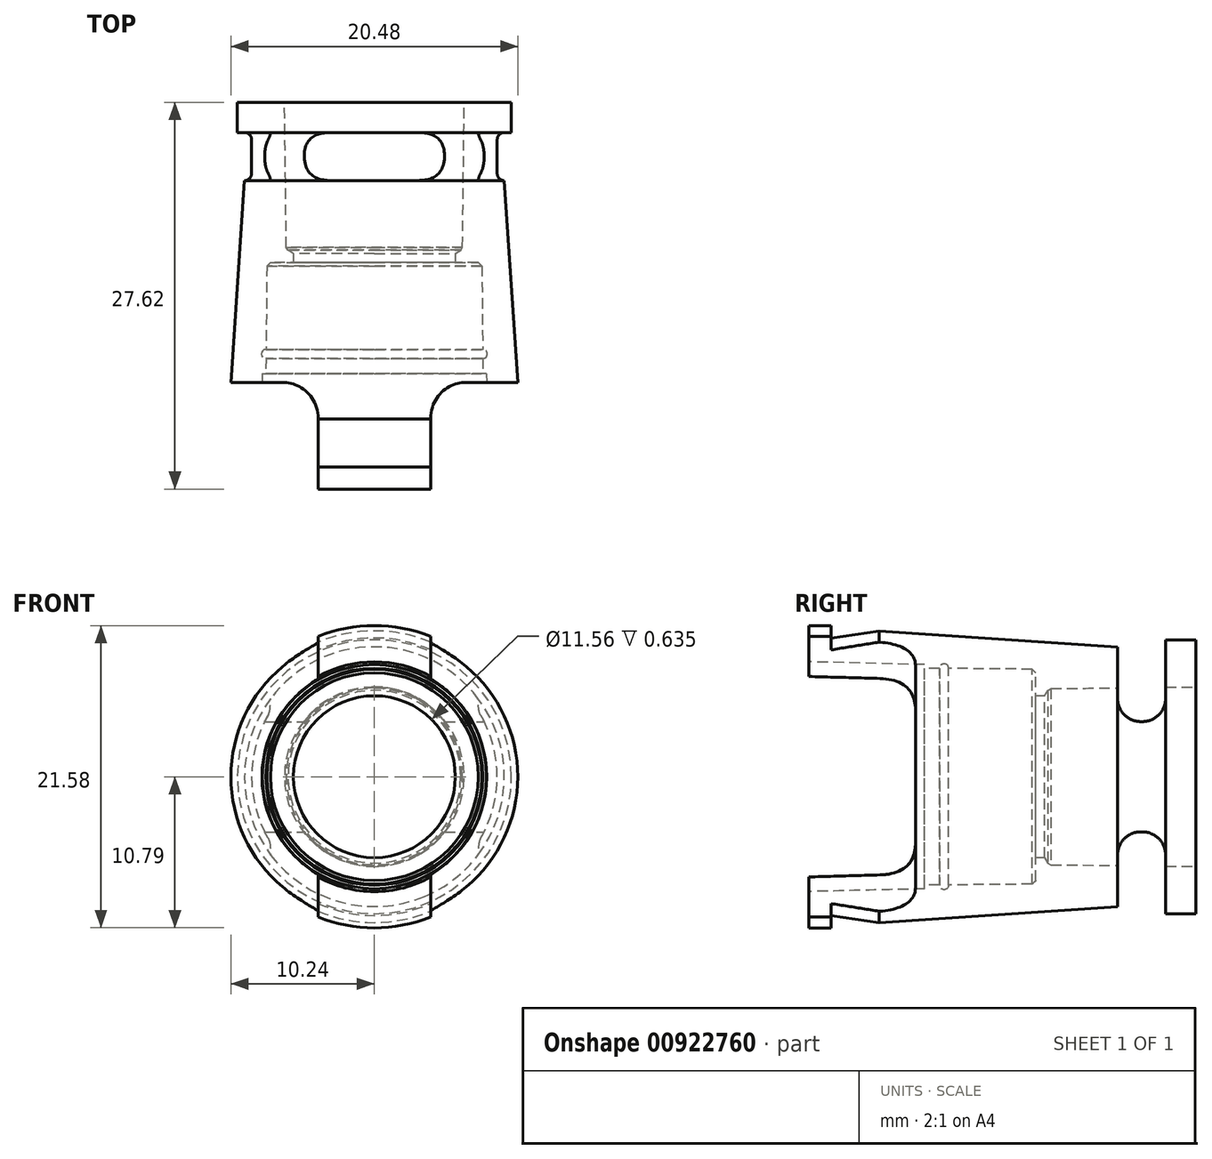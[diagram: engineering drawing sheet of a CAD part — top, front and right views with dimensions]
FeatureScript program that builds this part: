
annotation { "Feature Type Name" : "Feature", "Feature Type Description" : "" }
export const myFeature = defineFeature(function(context is Context, id is Id, definition is map)
    precondition{}
    {
        {
            var Q0;
            Q0=qCreatedBy(makeId("Right.planeOp"),FACE);
            var sketch = newSketch(context, id + "F0", { "sketchPlane" : qUnion([Q0])});
            skLineSegment(sketch, "E0.bottom", {"start": v(6.35, 6.41) * mm, "end": v(-6.35, 6.41) * mm, "construction": true});
            skLineSegment(sketch, "E0.top", {"start": v(6.35, -6.41) * mm, "end": v(-6.35, -6.41) * mm, "construction": true});
            skLineSegment(sketch, "E0.left", {"start": v(6.35, 6.41) * mm, "end": v(6.35, -6.41) * mm, "construction": true});
            skLineSegment(sketch, "E0.right", {"start": v(-6.35, 6.41) * mm, "end": v(-6.35, -6.41) * mm, "construction": true});
            skPoint(sketch, "E0.middle", {"position": v(0, 0) * mm});
            skLineSegment(sketch, "E1", {"start": v(-6.35, 6.41) * mm, "end": v(-6.35, 7.75) * mm});
            skLineSegment(sketch, "E2", {"start": v(-6.35, 6.41) * mm, "end": v(6.35, 6.41) * mm});
            skLineSegment(sketch, "E3", {"start": v(-6.35, 7.75) * mm, "end": v(-14.29, 7.75) * mm});
            skLineSegment(sketch, "E4", {"start": v(-14.29, 7.75) * mm, "end": v(-14.29, 8.2) * mm});
            skLineSegment(sketch, "E5", {"start": v(-14.29, 8.2) * mm, "end": v(-22.54, 8.2) * mm});
            skLineSegment(sketch, "E6", {"start": v(-6.35, 9.27) * mm, "end": v(-22.54, 9.27) * mm});
            skLineSegment(sketch, "E7", {"start": v(-22.54, 8.2) * mm, "end": v(-22.54, 9.27) * mm});
            skLineSegment(sketch, "E8", {"start": v(-6.35, 9.27) * mm, "end": v(6.35, 9.27) * mm});
            skLineSegment(sketch, "E9.bottom", {"start": v(-0.5, 8.76) * mm, "end": v(2.92, 8.76) * mm});
            skLineSegment(sketch, "E9.top", {"start": v(-0.5, 10.8) * mm, "end": v(2.92, 10.8) * mm});
            skLineSegment(sketch, "E9.left", {"start": v(-0.5, 8.76) * mm, "end": v(-0.5, 10.8) * mm});
            skLineSegment(sketch, "E9.right", {"start": v(2.92, 8.76) * mm, "end": v(2.92, 10.8) * mm});
            skLineSegment(sketch, "E10", {"start": v(0, 0) * mm, "end": v(6.35, 0) * mm});
            skLineSegment(sketch, "E11", {"start": v(-6.35, 6.41) * mm, "end": v(-6.35, 5.78) * mm});
            skLineSegment(sketch, "E12", {"start": v(-6.35, 5.78) * mm, "end": v(-5.72, 5.78) * mm});
            skLineSegment(sketch, "E13", {"start": v(-5.72, 5.78) * mm, "end": v(-5.33, 6.41) * mm});
            skLineSegment(sketch, "E14", {"start": v(5.08, 6.41) * mm, "end": v(5.08, 9.27) * mm});
            skLineSegment(sketch, "E15", {"start": v(-6.35, 7.67) * mm, "end": v(-14.29, 7.75) * mm});
            skLineSegment(sketch, "E16", {"start": v(-14.29, 8) * mm, "end": v(-22.54, 8.2) * mm});
            skLineSegment(sketch, "E17", {"start": v(-5.41, 6.29) * mm, "end": v(5.08, 6.41) * mm});
            skLineSegment(sketch, "E18", {"start": v(-22.54, 9.27) * mm, "end": v(-22.54, 10.8) * mm});
            skLineSegment(sketch, "E19", {"start": v(-22.54, 10.8) * mm, "end": v(-20.96, 10.8) * mm});
            skLineSegment(sketch, "E20", {"start": v(-20.96, 10.8) * mm, "end": v(-20.96, 9.27) * mm});
            skLineSegment(sketch, "E21", {"start": v(-17.53, 9.27) * mm, "end": v(-17.53, 10.41) * mm});
            skLineSegment(sketch, "E22", {"start": v(-17.53, 10.41) * mm, "end": v(-0.5, 9.27) * mm});
            skLineSegment(sketch, "E23", {"start": v(2.92, 9.78) * mm, "end": v(5.08, 9.78) * mm});
            skLineSegment(sketch, "E24", {"start": v(5.08, 9.78) * mm, "end": v(5.08, 9.27) * mm});
            skLineSegment(sketch, "E25", {"start": v(-17.53, 10.41) * mm, "end": v(-20.96, 9.9) * mm});
            skCircle(sketch, "E26", {"center": v(-12.9, 7.75) * mm, "radius": 0.32 * mm});
            skSolve(sketch);
        }
        {
            var Q0;
            Q0=makeQuery(id+"F0.imprint","IMPRINT",FACE,{"disambiguationData":[TD([[makeQuery(id+"F0.imprint","IMPRINT",EDGE,{"derivedFrom":sQuery(id+"F0.wireOp",EDGE,"E1")}),-1.0]])]});
            var Q1;
            {var subQ0=sQuery(id+"F0.wireOp",EDGE,"E11");Q1=makeQuery(id+"F0.imprint","IMPRINT",FACE,{"disambiguationData":[TD([[makeQuery(id+"F0.imprint","IMPRINT",EDGE,{"derivedFrom":subQ0}),1.0]])]});}
            var Q2;
            {var subQ3=sQuery(id+"F0.wireOp",EDGE,"E17");Q2=makeQuery(id+"F0.imprint","IMPRINT",FACE,{"disambiguationData":[TD([[makeQuery(id+"F0.imprint","IMPRINT",EDGE,{"derivedFrom":subQ3}),1.0]])]});}
            var Q3;
            {var subQ0=sQuery(id+"F0.wireOp",EDGE,"E3");Q3=makeQuery(id+"F0.imprint","IMPRINT",FACE,{"disambiguationData":[TD([[makeQuery(id+"F0.imprint","IMPRINT",EDGE,{"derivedFrom":subQ0}),1.0]])]});}
            var Q4;
            {var subQ0=sQuery(id+"F0.wireOp",EDGE,"E5");Q4=makeQuery(id+"F0.imprint","IMPRINT",FACE,{"disambiguationData":[TD([[makeQuery(id+"F0.imprint","IMPRINT",EDGE,{"derivedFrom":subQ0}),1.0]])]});}
            var Q5;
            {var subQ0=sQuery(id+"F0.wireOp",EDGE,"E18");Q5=makeQuery(id+"F0.imprint","IMPRINT",FACE,{"disambiguationData":[TD([[makeQuery(id+"F0.imprint","IMPRINT",EDGE,{"derivedFrom":subQ0}),-1.0]])]});}
            var Q6;
            {var subQ0=sQuery(id+"F0.wireOp",EDGE,"5LsXratz-BNPQ-VC7Z-SVJn-PDCCO9ljKIPs");Q6=makeQuery(id+"F0.imprint","IMPRINT",FACE,{"disambiguationData":[TD([[makeQuery(id+"F0.imprint","IMPRINT",EDGE,{"derivedFrom":subQ0}),1.0]])]});}
            var Q7;
            {var subQ3=sQuery(id+"F0.wireOp",EDGE,"E21");Q7=makeQuery(id+"F0.imprint","IMPRINT",FACE,{"disambiguationData":[TD([[makeQuery(id+"F0.imprint","IMPRINT",EDGE,{"derivedFrom":subQ3}),-1.0]])]});}
            var Q8;
            {var subQ1=sQuery(id+"F0.wireOp",EDGE,"E8");var subQ3=sQuery(id+"F0.wireOp",EDGE,"OCwKnorv-oSiF-PSZw-0uhv-YwaRGwNhvq4Y");var subQ4=makeQuery(id+"F0.imprint","INTERSECT",VERTEX,{"derivedFrom":[subQ1,subQ3]});Q8=makeQuery(id+"F0.imprint","IMPRINT",FACE,{"disambiguationData":[TD([[makeQuery(id+"F0.imprint","IMPRINT",EDGE,{"disambiguationData":[TD([[subQ4,1.0]])],"derivedFrom":subQ3}),1.0]])]});}
            var Q9;
            {var subQ4=sQuery(id+"F0.wireOp",EDGE,"E23");Q9=makeQuery(id+"F0.imprint","IMPRINT",FACE,{"disambiguationData":[TD([[makeQuery(id+"F0.imprint","IMPRINT",EDGE,{"derivedFrom":subQ4}),-1.0]])]});}
            var Q10;
            {var subQ3=sQuery(id+"F0.wireOp",EDGE,"E21");Q10=makeQuery(id+"F0.imprint","IMPRINT",FACE,{"disambiguationData":[TD([[makeQuery(id+"F0.imprint","IMPRINT",EDGE,{"derivedFrom":subQ3}),1.0]])]});}
            var Q11;
            {var subQ0=sQuery(id+"F0.wireOp",EDGE,"E26");var subQ1=sQuery(id+"F0.wireOp",EDGE,"E3");var subQ2=makeQuery(id+"F0.imprint","INTERSECT",VERTEX,{"disambiguationData":[OD(0.0)],"derivedFrom":[subQ1,subQ0]});Q11=makeQuery(id+"F0.imprint","IMPRINT",FACE,{"disambiguationData":[TD([[makeQuery(id+"F0.imprint","IMPRINT",EDGE,{"disambiguationData":[TD([[subQ2,-1.0]])],"derivedFrom":subQ1}),-1.0]])]});}
            var Q12;
            {var subQ0=sQuery(id+"F0.wireOp",EDGE,"E3");var subQ1=sQuery(id+"F0.wireOp",EDGE,"E1");var subQ2=makeQuery(id+"F0.imprint","INTERSECT",VERTEX,{"derivedFrom":[subQ1,subQ0]});Q12=makeQuery(id+"F0.imprint","IMPRINT",FACE,{"disambiguationData":[TD([[makeQuery(id+"F0.imprint","IMPRINT",EDGE,{"disambiguationData":[TD([[subQ2,1.0]])],"derivedFrom":subQ1}),1.0]])]});}
            var Q13;
            {var subQ0=sQuery(id+"F0.wireOp",EDGE,"E26");var subQ1=sQuery(id+"F0.wireOp",EDGE,"E3");var subQ2=makeQuery(id+"F0.imprint","INTERSECT",VERTEX,{"disambiguationData":[OD(0.0)],"derivedFrom":[subQ1,subQ0]});Q13=makeQuery(id+"F0.imprint","IMPRINT",FACE,{"disambiguationData":[TD([[makeQuery(id+"F0.imprint","IMPRINT",EDGE,{"disambiguationData":[TD([[subQ2,-1.0]])],"derivedFrom":subQ1}),1.0]])]});}
            var Q14;
            Q14=sQuery(id+"F0.wireOp",EDGE,"E10");
            revolve(context, id + "F1", {"surfaceOperationType" : NewSurfaceOperationType.NEW, "entities" : qUnion([Q0, Q1, Q2, Q3, Q4, Q5, Q6, Q7, Q8, Q9, Q10, Q11, Q12, Q13]), "axis" : qUnion([Q14]), "revolveType" : RevolveType.FULL});
        }
        {
            var Q0;
            Q0=makeQuery(id+"F1.opRevolve","SWEPT_FACE",FACE,{"disambiguationData":[OSD([sQuery(id+"F0.wireOp",EDGE,"E7"),sQuery(id+"F0.wireOp",EDGE,"E18")])]});
            var sketch = newSketch(context, id + "F2", { "sketchPlane" : qUnion([Q0])});
            skLineSegment(sketch, "E27.bottom", {"start": v(-12.14, 12.7) * mm, "end": v(-4.01, 12.7) * mm});
            skLineSegment(sketch, "E27.top", {"start": v(-12.14, -12.7) * mm, "end": v(-4.01, -12.7) * mm});
            skLineSegment(sketch, "E27.left", {"start": v(-12.14, 12.7) * mm, "end": v(-12.14, -12.7) * mm});
            skLineSegment(sketch, "E27.right", {"start": v(-4.01, 12.7) * mm, "end": v(-4.01, -12.7) * mm});
            skPoint(sketch, "E27.middle", {"position": v(-8.08, 0) * mm});
            skLineSegment(sketch, "E28.1.0", {"start": v(12.14, -12.7) * mm, "end": v(12.14, 12.7) * mm});
            skLineSegment(sketch, "E28.1.1", {"start": v(12.14, -12.7) * mm, "end": v(4.01, -12.7) * mm});
            skLineSegment(sketch, "E28.1.2", {"start": v(12.14, 12.7) * mm, "end": v(4.01, 12.7) * mm});
            skLineSegment(sketch, "E28.1.3", {"start": v(4.01, -12.7) * mm, "end": v(4.01, 12.7) * mm});
            skPoint(sketch, "E28.center", {"position": v(0, 0) * mm});
            skSolve(sketch);
        }
        {
            var Q0;
            Q0=qSketchRegion(id+"F2",true);
            extrude(context, id + "F3", {"entities" : qUnion([Q0]), "operationType" : NewBodyOperationType.REMOVE, "oppositeDirection" : true, "depth" : 7.62 * mm, "offsetDistance" : 25.4 * mm});
        }
        {
            var Q0;
            Q0=makeQuery(id+"F1.opRevolve","SWEPT_EDGE",EDGE,{"disambiguationData":[OSD([sQuery(id+"F0.wireOp",EDGE,"E13"),sQuery(id+"F0.wireOp",EDGE,"E17")])]});
            var Q1;
            Q1=makeQuery(id+"F1.opRevolve","SWEPT_EDGE",EDGE,{"disambiguationData":[OSD([sQuery(id+"F0.wireOp",EDGE,"E1"),sQuery(id+"F0.wireOp",EDGE,"E15")])]});
            chamfer(context, id + "F4", {"entities" : qUnion([Q0, Q1]), "width" : 0.25 * mm, "tangentPropagation" : true});
        }
        {
            var Q0;
            Q0=makeQuery(id+"F3.boolean.opBoolean","COPY",EDGE,{"disambiguationData":[OD(1.0)],"derivedFrom":makeQuery(id+"F3.opExtrude","CAP_EDGE",EDGE,{"disambiguationData":[OSD([sQuery(id+"F2.wireOp",EDGE,"E28.1.3")])],"isStart":false})});
            var Q1;
            Q1=makeQuery(id+"Fx99BmHJkbAKeAa_1.boolean.opBoolean","COPY",EDGE,{"disambiguationData":[OD(1.0)],"derivedFrom":makeQuery(id+"Fx99BmHJkbAKeAa_1.opExtrude","CAP_EDGE",EDGE,{"disambiguationData":[OSD([sQuery(id+"F9ZcsWvbm63dtT8_1.wireOp",EDGE,"Iu0nxSGF-gViM-aj9T-gyUk-CUqZmY8DqRDU.right")])],"isStart":false})});
            var Q2;
            Q2=makeQuery(id+"Fx99BmHJkbAKeAa_1.boolean.opBoolean","COPY",EDGE,{"disambiguationData":[OD(0.0)],"derivedFrom":makeQuery(id+"Fx99BmHJkbAKeAa_1.opExtrude","CAP_EDGE",EDGE,{"disambiguationData":[OSD([sQuery(id+"F9ZcsWvbm63dtT8_1.wireOp",EDGE,"Iu0nxSGF-gViM-aj9T-gyUk-CUqZmY8DqRDU.right")])],"isStart":false})});
            var Q3;
            Q3=makeQuery(id+"F3.boolean.opBoolean","COPY",EDGE,{"disambiguationData":[OD(0.0)],"derivedFrom":makeQuery(id+"F3.opExtrude","CAP_EDGE",EDGE,{"disambiguationData":[OSD([sQuery(id+"F2.wireOp",EDGE,"E28.1.3")])],"isStart":false})});
            var Q4;
            Q4=makeQuery(id+"F3.boolean.opBoolean","COPY",EDGE,{"disambiguationData":[OD(1.0)],"derivedFrom":makeQuery(id+"F3.opExtrude","CAP_EDGE",EDGE,{"disambiguationData":[OSD([sQuery(id+"F2.wireOp",EDGE,"E27.right")])],"isStart":false})});
            var Q5;
            Q5=makeQuery(id+"F3.boolean.opBoolean","COPY",EDGE,{"disambiguationData":[OD(0.0)],"derivedFrom":makeQuery(id+"F3.opExtrude","CAP_EDGE",EDGE,{"disambiguationData":[OSD([sQuery(id+"F2.wireOp",EDGE,"E27.right")])],"isStart":false})});
            var Q6;
            Q6=makeQuery(id+"Fx99BmHJkbAKeAa_1.boolean.opBoolean","COPY",EDGE,{"disambiguationData":[OD(0.0)],"derivedFrom":makeQuery(id+"Fx99BmHJkbAKeAa_1.opExtrude","CAP_EDGE",EDGE,{"disambiguationData":[OSD([sQuery(id+"F9ZcsWvbm63dtT8_1.wireOp",EDGE,"046a7c88-4249-47b8-9f9c-165aad1a66e0.1.3")])],"isStart":false})});
            var Q7;
            Q7=makeQuery(id+"Fx99BmHJkbAKeAa_1.boolean.opBoolean","COPY",EDGE,{"disambiguationData":[OD(1.0)],"derivedFrom":makeQuery(id+"Fx99BmHJkbAKeAa_1.opExtrude","CAP_EDGE",EDGE,{"disambiguationData":[OSD([sQuery(id+"F9ZcsWvbm63dtT8_1.wireOp",EDGE,"046a7c88-4249-47b8-9f9c-165aad1a66e0.1.3")])],"isStart":false})});
            fillet(context, id + "F5", {"entities" : qUnion([Q0, Q1, Q2, Q3, Q4, Q5, Q6, Q7]), "radius" : 2.54 * mm, "tangentPropagation" : true, "allowEdgeOverflow" : false});
        }
        {
            var Q0;
            {var subQ0=sQuery(id+"F0.wireOp",EDGE,"E26");var subQ1=sQuery(id+"F0.wireOp",EDGE,"E15");var subQ2=makeQuery(id+"F0.imprint","INTERSECT",VERTEX,{"disambiguationData":[OD(0.0)],"derivedFrom":[subQ1,subQ0]});Q0=makeQuery(id+"F0.imprint","IMPRINT",FACE,{"disambiguationData":[TD([[makeQuery(id+"F0.imprint","IMPRINT",EDGE,{"disambiguationData":[TD([[subQ2,-1.0]])],"derivedFrom":subQ1}),1.0]])]});}
            var Q1;
            {var subQ0=sQuery(id+"F0.wireOp",EDGE,"E26");var subQ1=sQuery(id+"F0.wireOp",EDGE,"E3");var subQ2=makeQuery(id+"F0.imprint","INTERSECT",VERTEX,{"disambiguationData":[OD(0.0)],"derivedFrom":[subQ1,subQ0]});Q1=makeQuery(id+"F0.imprint","IMPRINT",FACE,{"disambiguationData":[TD([[makeQuery(id+"F0.imprint","IMPRINT",EDGE,{"disambiguationData":[TD([[subQ2,-1.0]])],"derivedFrom":subQ1}),1.0]])]});}
            var Q2;
            Q2=sQuery(id+"F0.wireOp",EDGE,"E10");
            revolve(context, id + "F6", {"operationType" : NewBodyOperationType.ADD, "surfaceOperationType" : NewSurfaceOperationType.NEW, "entities" : qUnion([Q0, Q1]), "axis" : qUnion([Q2]), "revolveType" : RevolveType.ONE_DIRECTION, "angle" : 180 * degree});
        }
        {
            var Q0;
            Q0=qCreatedBy(makeId("Right.planeOp"),FACE);
            var sketch = newSketch(context, id + "F7", { "sketchPlane" : qUnion([Q0])});
            skLineSegment(sketch, "E29.0", {"start": v(2.92, -8.76) * mm, "end": v(2.92, 8.76) * mm, "construction": true});
            skLineSegment(sketch, "E29.1", {"start": v(-0.5, -8.76) * mm, "end": v(-0.5, 8.76) * mm, "construction": true});
            skLineSegment(sketch, "E30", {"start": v(2.92, 8.76) * mm, "end": v(-0.5, 8.76) * mm, "construction": true});
            skLineSegment(sketch, "E31", {"start": v(2.92, -8.76) * mm, "end": v(-0.5, -8.76) * mm, "construction": true});
            skLineSegment(sketch, "E32.bottom", {"start": v(-0.5, 13.59) * mm, "end": v(2.92, 13.59) * mm});
            skLineSegment(sketch, "E32.top", {"start": v(-0.5, 3.94) * mm, "end": v(2.92, 3.94) * mm});
            skLineSegment(sketch, "E32.left", {"start": v(-0.5, 13.59) * mm, "end": v(-0.5, 3.94) * mm});
            skLineSegment(sketch, "E32.right", {"start": v(2.92, 13.59) * mm, "end": v(2.92, 3.94) * mm});
            skPoint(sketch, "E32.middle", {"position": v(1.2, 8.76) * mm});
            skLineSegment(sketch, "E33.bottom", {"start": v(-0.5, -3.94) * mm, "end": v(2.92, -3.94) * mm});
            skLineSegment(sketch, "E33.top", {"start": v(-0.5, -13.59) * mm, "end": v(2.92, -13.59) * mm});
            skLineSegment(sketch, "E33.left", {"start": v(-0.5, -3.94) * mm, "end": v(-0.5, -13.59) * mm});
            skLineSegment(sketch, "E33.right", {"start": v(2.92, -3.94) * mm, "end": v(2.92, -13.59) * mm});
            skPoint(sketch, "E33.middle", {"position": v(1.2, -8.76) * mm});
            skSolve(sketch);
        }
        {
            var Q0;
            Q0 = qSketchRegion(id + "F7", true);
            extrude(context, id + "F8", {"entities" : qUnion([Q0]), "operationType" : NewBodyOperationType.REMOVE, "endBound" : BoundingType.SYMMETRIC, "oppositeDirection" : true, "depth" : 38.1 * mm, "offsetDistance" : 25.4 * mm});
        }
        {
            var Q0;
            Q0=makeQuery(id+"F8.boolean.opBoolean","SPLIT",EDGE,{"disambiguationData":[OD(1.0)],"derivedFrom":makeQuery(id+"F1.opRevolve","SWEPT_EDGE",EDGE,{"disambiguationData":[OSD([sQuery(id+"F0.wireOp",EDGE,"E9.bottom"),sQuery(id+"F0.wireOp",EDGE,"E9.left")])]})});
            var Q1;
            Q1=makeQuery(id+"F8.boolean.opBoolean","SPLIT",EDGE,{"disambiguationData":[OD(0.0)],"derivedFrom":makeQuery(id+"F1.opRevolve","SWEPT_EDGE",EDGE,{"disambiguationData":[OSD([sQuery(id+"F0.wireOp",EDGE,"E9.bottom"),sQuery(id+"F0.wireOp",EDGE,"E9.left")])]})});
            var Q2;
            Q2=makeQuery(id+"F8.boolean.opBoolean","SPLIT",EDGE,{"disambiguationData":[OD(0.0)],"derivedFrom":makeQuery(id+"F1.opRevolve","SWEPT_EDGE",EDGE,{"disambiguationData":[OSD([sQuery(id+"F0.wireOp",EDGE,"E9.bottom"),sQuery(id+"F0.wireOp",EDGE,"E9.right")])]})});
            var Q3;
            Q3=makeQuery(id+"F8.boolean.opBoolean","SPLIT",EDGE,{"disambiguationData":[OD(1.0)],"derivedFrom":makeQuery(id+"F1.opRevolve","SWEPT_EDGE",EDGE,{"disambiguationData":[OSD([sQuery(id+"F0.wireOp",EDGE,"E9.bottom"),sQuery(id+"F0.wireOp",EDGE,"E9.right")])]})});
            fillet(context, id + "F9", {"entities" : qUnion([Q0, Q1, Q2, Q3]), "radius" : 0.5 * mm, "tangentPropagation" : true, "allowEdgeOverflow" : false});
        }
        {
            var Q0;
            Q0=makeQuery(id+"F8.boolean.opBoolean","COPY",EDGE,{"disambiguationData":[OD(0.0)],"derivedFrom":makeQuery(id+"F8.opExtrude","SWEPT_EDGE",EDGE,{"disambiguationData":[OSD([sQuery(id+"F7.wireOp",EDGE,"E33.bottom"),sQuery(id+"F7.wireOp",EDGE,"E33.left")])]})});
            var Q1;
            Q1=makeQuery(id+"F8.boolean.opBoolean","COPY",EDGE,{"disambiguationData":[OD(0.0)],"derivedFrom":makeQuery(id+"F8.opExtrude","SWEPT_EDGE",EDGE,{"disambiguationData":[OSD([sQuery(id+"F7.wireOp",EDGE,"E33.bottom"),sQuery(id+"F7.wireOp",EDGE,"E33.right")])]})});
            var Q2;
            Q2=makeQuery(id+"F8.boolean.opBoolean","COPY",EDGE,{"disambiguationData":[OD(0.0)],"derivedFrom":makeQuery(id+"F8.opExtrude","SWEPT_EDGE",EDGE,{"disambiguationData":[OSD([sQuery(id+"F7.wireOp",EDGE,"E32.top"),sQuery(id+"F7.wireOp",EDGE,"E32.left")])]})});
            var Q3;
            Q3=makeQuery(id+"F8.boolean.opBoolean","COPY",EDGE,{"disambiguationData":[OD(0.0)],"derivedFrom":makeQuery(id+"F8.opExtrude","SWEPT_EDGE",EDGE,{"disambiguationData":[OSD([sQuery(id+"F7.wireOp",EDGE,"E32.top"),sQuery(id+"F7.wireOp",EDGE,"E32.right")])]})});
            var Q4;
            Q4=makeQuery(id+"F8.boolean.opBoolean","COPY",EDGE,{"disambiguationData":[OD(1.0)],"derivedFrom":makeQuery(id+"F8.opExtrude","SWEPT_EDGE",EDGE,{"disambiguationData":[OSD([sQuery(id+"F7.wireOp",EDGE,"E32.top"),sQuery(id+"F7.wireOp",EDGE,"E32.left")])]})});
            var Q5;
            Q5=makeQuery(id+"F8.boolean.opBoolean","COPY",EDGE,{"disambiguationData":[OD(1.0)],"derivedFrom":makeQuery(id+"F8.opExtrude","SWEPT_EDGE",EDGE,{"disambiguationData":[OSD([sQuery(id+"F7.wireOp",EDGE,"E32.top"),sQuery(id+"F7.wireOp",EDGE,"E32.right")])]})});
            var Q6;
            Q6=makeQuery(id+"F8.boolean.opBoolean","COPY",EDGE,{"disambiguationData":[OD(1.0)],"derivedFrom":makeQuery(id+"F8.opExtrude","SWEPT_EDGE",EDGE,{"disambiguationData":[OSD([sQuery(id+"F7.wireOp",EDGE,"E33.bottom"),sQuery(id+"F7.wireOp",EDGE,"E33.left")])]})});
            var Q7;
            Q7=makeQuery(id+"F8.boolean.opBoolean","COPY",EDGE,{"disambiguationData":[OD(1.0)],"derivedFrom":makeQuery(id+"F8.opExtrude","SWEPT_EDGE",EDGE,{"disambiguationData":[OSD([sQuery(id+"F7.wireOp",EDGE,"E33.bottom"),sQuery(id+"F7.wireOp",EDGE,"E33.right")])]})});
            fillet(context, id + "F10", {"entities" : qUnion([Q0, Q1, Q2, Q3, Q4, Q5, Q6, Q7]), "radius" : 1.65 * mm, "tangentPropagation" : true, "allowEdgeOverflow" : false});
        }
    });
